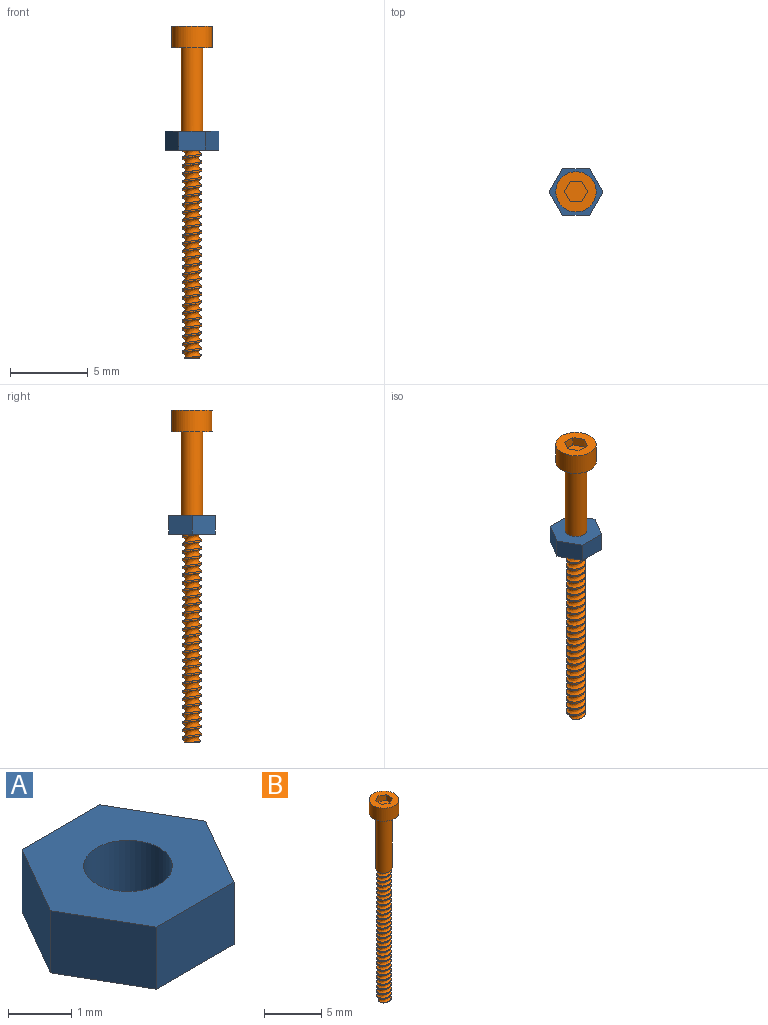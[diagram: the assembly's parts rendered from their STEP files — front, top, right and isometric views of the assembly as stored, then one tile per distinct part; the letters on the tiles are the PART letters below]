
ASSEMBLY  parts=2 mates=1
PART A: 9 faces, bbox 3.5x3x1.2 mm
  f0: plane 1.5x1.2mm, normal (0.87,0.5,0), area 2.1mm2, adj f1,f6,f7,f8
  f1: plane 1.73x1.2mm, normal (0,1,0), area 2.1mm2, adj f0,f2,f7,f8
  f2: plane 1.5x1.2mm, normal (-0.87,0.5,0), area 2.1mm2, adj f1,f3,f7,f8
  f3: plane 1.5x1.2mm, normal (-0.87,-0.5,0), area 2.1mm2, adj f2,f4,f7,f8
  f4: plane 1.73x1.2mm, normal (0,-1,0), area 2.1mm2, adj f3,f6,f7,f8
  f5: cylinder r=0.7mm len=1.4mm, axis (0,0,-1), area 5.3mm2, adj f7,f8
  f6: plane 1.5x1.2mm, normal (0.87,-0.5,0), area 2.1mm2, adj f0,f4,f7,f8
  f7: plane 3.46x3mm, normal (0,0,1), area 6.3mm2, adj f0,f1,f2,f3,f4,f5,f6
  f8: plane 3.46x3mm, normal (0,0,-1), area 6.3mm2, adj f0,f1,f2,f3,f4,f5,f6
PART B: 18 faces, bbox 2.7x2.7x21.7 mm
  f0: cylinder r=0.7mm len=6mm, axis (0,0,1), area 26.2mm2, adj f1,f2,f15,f16
  f1: plane 1.43x1.23mm, normal (0,0,-1), area 0.2mm2, adj f0,f6,f15,f16
  f2: plane 2.6x2.6mm, normal (0,0,-1), area 3.8mm2, adj f0,f3
  f3: cylinder r=1.3mm len=2.6mm, axis (0,0,1), area 11.4mm2, adj f2,f4
  f4: plane 2.6x2.6mm, normal (0,0,1), area 3.8mm2, adj f3,f7,f8,f9,f10,f11,f12
  f5: plane 1.02x1.01mm, normal (0,0,-1), area 0.7mm2, adj f14,f16,f17
  f6: cylinder r=0.63mm len=13.86mm, axis (0,0,1), area 2.7mm2, adj f1,f14,f15,f16,f17
  f7: plane 0.65x0.6mm, normal (-0.5,0.87,0), area 0.5mm2, adj f4,f8,f12,f13
  f8: plane 0.75x0.6mm, normal (-1,0,0), area 0.5mm2, adj f4,f7,f9,f13
  f9: plane 0.65x0.6mm, normal (-0.5,-0.87,0), area 0.5mm2, adj f4,f8,f10,f13
  f10: plane 0.65x0.6mm, normal (0.5,-0.87,0), area 0.5mm2, adj f4,f9,f11,f13
  f11: plane 0.75x0.6mm, normal (1,0,0), area 0.5mm2, adj f4,f10,f12,f13
  f12: plane 0.65x0.6mm, normal (0.5,0.87,0), area 0.5mm2, adj f4,f7,f11,f13
  f13: plane 1.5x1.3mm, normal (0,0,1), area 1.5mm2, adj f7,f8,f9,f10,f11,f12
  f14: plane 0.26x0.26mm, normal (0,1,0), area 0mm2, adj f5,f6,f16,f17
  f15: plane 0.49x0.36mm, normal (0,-1,0), area 0.1mm2, adj f0,f1,f6,f16
  f16: bspline ~14.4x2.38mm, area 55.7mm2, adj f0,f1,f5,f6,f14,f15,f17
  f17: cone r=0.63mm half-angle=45deg, axis (0,0,1), area 0.4mm2, adj f5,f6,f14,f16
PLACE A t=(10.4,7.59,9.27)mm fixed
PLACE B rot(axis=(0,0,1),90deg) t=(10.4,7.59,15.87)mm
MATE cylindrical B.f0 <-> A.f5  axis (0,0,1) through (10.4,7.59,9.87)mm
